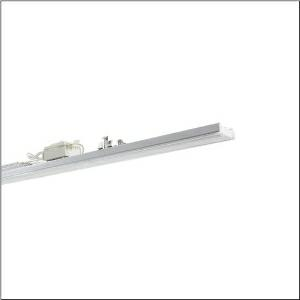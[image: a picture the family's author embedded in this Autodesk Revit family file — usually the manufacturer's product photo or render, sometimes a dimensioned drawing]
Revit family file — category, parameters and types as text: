
# Revit family: licross_r__21_recessed_mo_52tl197n48xg_c19d
name_source: partatom
category: Lighting Fixtures
units: mm (PartAtom-declared; Revit-internal decimal feet)

## family parameters
Cut with Voids When Loaded = No
Host = Face
Light Source = No
Part Type = Normal
Room Calculation Point = No
Round Connector Dimension = Use Diameter
Shared = No

## types (1)
- Licross® 21 Recessed MO (1 x LED, 8450 lm, 47.9 W, 4000K)
    Apparent Load = 48 VA
    CIE Flux Codes = 55 90 98 100 100
    Color Rendering = 80
    Color Temperature = 4000K
    Default Elevation = 1800 mm
    Description = Licross® 21 Recessed MO, luminaire insert, of sheet steel, galvanised, coil coated, white, length: 1.500mm, width: 66mm, height: 67mm, LED rated luminous flux: 8.450lm, light colour: 840, control gear: ON/OFF, with plug, 3-pole, with phase selection, mains connection: 220..240V, AC, 50/60Hz, rated input power: 48W, halogen-free wiring, primary light control with lens, of plastic, primary optical cover: cover, of PMMA, light emission: direct distribution, primary light characteristic: double asymmetric, protection rating (complete): IP40, insulation class (complete): insulation class I (protective earthing), certification: CE, ENEC, VDE, UKCA, protection symbol: D if used in an environment without relevant dust loads with corresponding accessories, impact resistance: IK06, permissible ambient temperature for indoor applications: -35..+40°C, corresponds to IFS (International Featured Standards) requirements for safety and quality in the food industry, reducing of maximum allowable ambient temperature of 5°C with ceiling mounting, LABS conformity tested according to VDMA 24364:2018-05, packaging unit: 1 piece
    Height = 58 mm
    Lamp = 1 x LED
    Lamp Light Flux = 8450 lm
    Lamp Power = 47.9 W
    Lamp count = 1
    Length = 1500 mm
    Luminous efficacy = 176 lm/W
    Manufacturer = Siteco
    ModVariant = No
    Model = 52TL197N48XG
    Mounting Place = Ceiling
    Mounting Type = Pendant
    Number of Poles = 1
    OnlyDefault = Yes
    Power Factor = 1
    Product Name = Licross® 21 Recessed MO
    Product group = luminaire insert
    ProductGroupID = 902
    Protection Class = Protection class I
    Protection Degree = IP 40
    RLX_Detail_Level = 1
    RLX_Emergency_Light_Flux = 0 lm
    RLX_Emergency_Type = 0
    RLX_Emergency_Type_DB = No
    RlxData = <blob elided: 20901 chars, md5=8e8660ad>
    Socket = socket
    Standby Power = 0 W
    System Light Flux = 8450 lm
    System Power = 48 W
    Type Comments = Product without accessories
    Type Image = l_1296930.jpg
    URL = http://relux.com
    VarID = ---
    Voltage = 0 V
    Weight = 0.00 kg
    Width = 66 mm

## geometry (parser evidence)
native form markers: Blend x4, Sweep x10
no freeform markers — native parametric forms only
